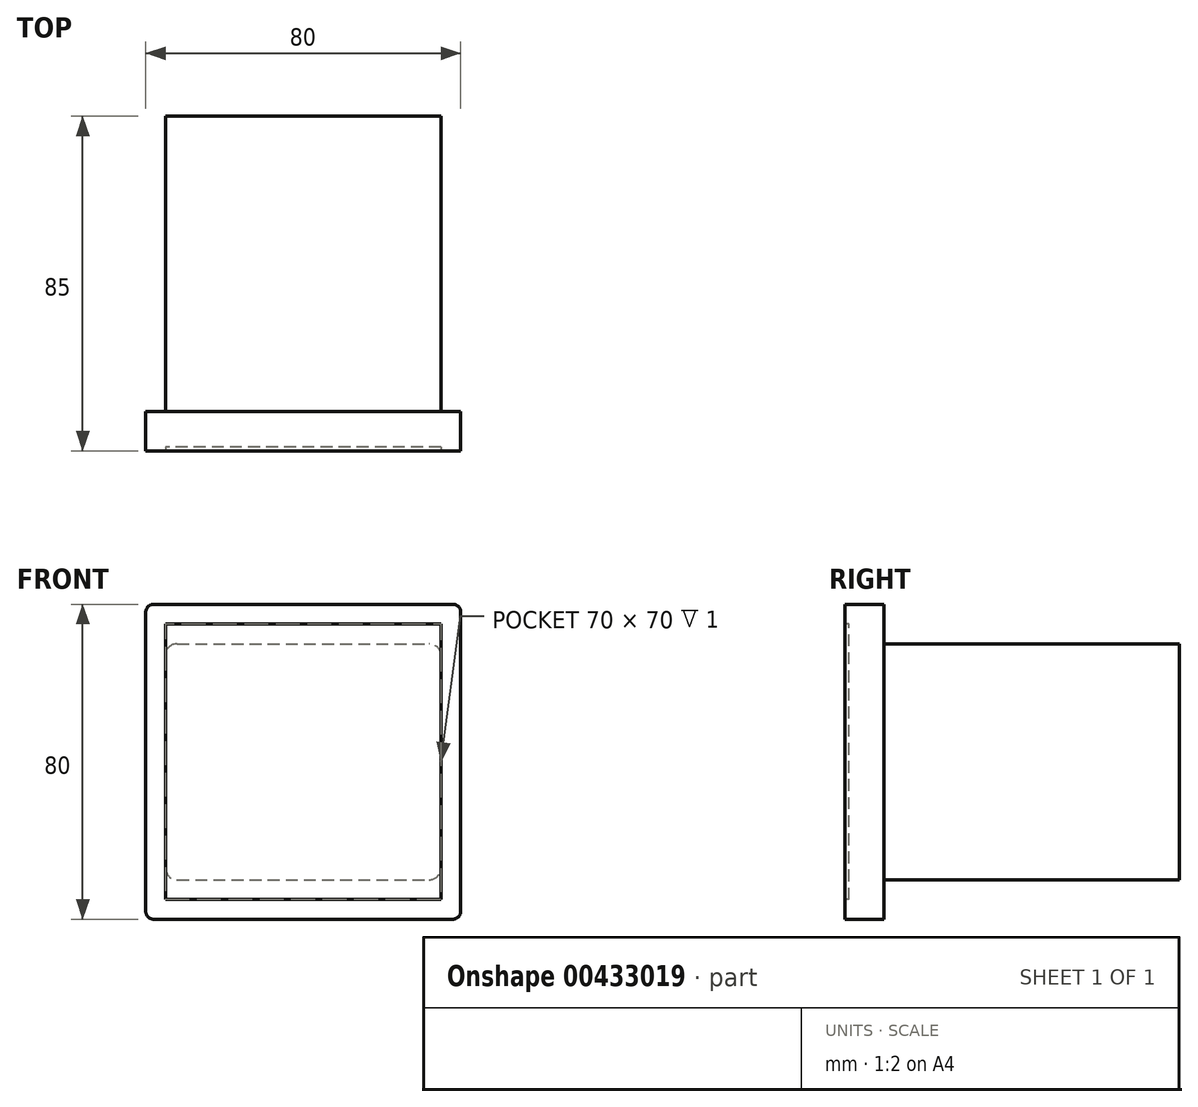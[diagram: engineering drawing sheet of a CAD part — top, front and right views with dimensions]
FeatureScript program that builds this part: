
annotation { "Feature Type Name" : "Feature", "Feature Type Description" : "" }
export const myFeature = defineFeature(function(context is Context, id is Id, definition is map)
    precondition{}
    {
        {
            var Q0;
            Q0=qCreatedBy(makeId("Front.planeOp"),FACE);
            var sketch = newSketch(context, id + "F0", { "sketchPlane" : qUnion([Q0])});
            skLineSegment(sketch, "E0.bottom", {"start": v(40, -40) * mm, "end": v(-40, -40) * mm});
            skLineSegment(sketch, "E0.top", {"start": v(40, 40) * mm, "end": v(-40, 40) * mm});
            skLineSegment(sketch, "E0.left", {"start": v(40, -40) * mm, "end": v(40, 40) * mm});
            skLineSegment(sketch, "E0.right", {"start": v(-40, -40) * mm, "end": v(-40, 40) * mm});
            skPoint(sketch, "E0.middle", {"position": v(0, 0) * mm});
            skSolve(sketch);
        }
        {
            var Q0;
            Q0 = qSketchRegion(id + "F0", true);
            extrude(context, id + "F1", {"entities" : qUnion([Q0]), "depth" : 10 * mm});
        }
        {
            var Q0;
            Q0=makeQuery(id+"F1.opExtrude","SWEPT_EDGE",EDGE,{"disambiguationData":[OSD([sQuery(id+"F0.wireOp",EDGE,"E0.top"),sQuery(id+"F0.wireOp",EDGE,"E0.right")])]});
            var Q1;
            Q1=makeQuery(id+"F1.opExtrude","SWEPT_EDGE",EDGE,{"disambiguationData":[OSD([sQuery(id+"F0.wireOp",EDGE,"E0.top"),sQuery(id+"F0.wireOp",EDGE,"E0.left")])]});
            var Q2;
            Q2=makeQuery(id+"F1.opExtrude","SWEPT_EDGE",EDGE,{"disambiguationData":[OSD([sQuery(id+"F0.wireOp",EDGE,"E0.bottom"),sQuery(id+"F0.wireOp",EDGE,"E0.left")])]});
            var Q3;
            Q3=makeQuery(id+"F1.opExtrude","SWEPT_EDGE",EDGE,{"disambiguationData":[OSD([sQuery(id+"F0.wireOp",EDGE,"E0.bottom"),sQuery(id+"F0.wireOp",EDGE,"E0.right")])]});
            fillet(context, id + "F2", {"entities" : qUnion([Q0, Q1, Q2, Q3]), "radius" : 2 * mm, "tangentPropagation" : true, "allowEdgeOverflow" : false});
        }
        {
            var Q0;
            Q0=makeQuery(id+"F1.opExtrude","CAP_FACE",FACE,{"disambiguationData":[OSD([sQuery(id+"F0.wireOp",EDGE,"E0.bottom"),sQuery(id+"F0.wireOp",EDGE,"E0.top"),sQuery(id+"F0.wireOp",EDGE,"E0.left"),sQuery(id+"F0.wireOp",EDGE,"E0.right")])],"isStart":false});
            var sketch = newSketch(context, id + "F3", { "sketchPlane" : qUnion([Q0])});
            skLineSegment(sketch, "E1.bottom", {"start": v(35, -35) * mm, "end": v(-35, -35) * mm});
            skLineSegment(sketch, "E1.top", {"start": v(35, 35) * mm, "end": v(-35, 35) * mm});
            skLineSegment(sketch, "E1.left", {"start": v(35, -35) * mm, "end": v(35, 35) * mm});
            skLineSegment(sketch, "E1.right", {"start": v(-35, -35) * mm, "end": v(-35, 35) * mm});
            skPoint(sketch, "E1.middle", {"position": v(0, 0) * mm});
            skSolve(sketch);
        }
        {
            var Q0;
            Q0=makeQuery(id+"F3.imprint","IMPRINT",FACE,{"disambiguationData":[TD([[makeQuery(id+"F3.imprint","IMPRINT",EDGE,{"derivedFrom":sQuery(id+"F3.wireOp",EDGE,"E1.bottom")}),-1.0]])]});
            extrude(context, id + "F4", {"entities" : qUnion([Q0]), "operationType" : NewBodyOperationType.REMOVE, "oppositeDirection" : true, "depth" : 1 * mm});
        }
        {
            var Q0;
            Q0=makeQuery(id+"F1.opExtrude","CAP_FACE",FACE,{"disambiguationData":[OSD([sQuery(id+"F0.wireOp",EDGE,"E0.bottom"),sQuery(id+"F0.wireOp",EDGE,"E0.top"),sQuery(id+"F0.wireOp",EDGE,"E0.left"),sQuery(id+"F0.wireOp",EDGE,"E0.right")])],"isStart":true});
            var sketch = newSketch(context, id + "F5", { "sketchPlane" : qUnion([Q0])});
            skLineSegment(sketch, "E2.bottom", {"start": v(35, -30) * mm, "end": v(-35, -30) * mm});
            skLineSegment(sketch, "E2.top", {"start": v(35, 30) * mm, "end": v(-35, 30) * mm});
            skLineSegment(sketch, "E2.left", {"start": v(35, -30) * mm, "end": v(35, 30) * mm});
            skLineSegment(sketch, "E2.right", {"start": v(-35, -30) * mm, "end": v(-35, 30) * mm});
            skPoint(sketch, "E2.middle", {"position": v(0, 0) * mm});
            skSolve(sketch);
        }
        {
            var Q0;
            Q0=makeQuery(id+"F5.imprint","IMPRINT",FACE,{"disambiguationData":[TD([[makeQuery(id+"F5.imprint","IMPRINT",EDGE,{"derivedFrom":sQuery(id+"F5.wireOp",EDGE,"E2.bottom")}),-1.0]])]});
            extrude(context, id + "F6", {"entities" : qUnion([Q0]), "operationType" : NewBodyOperationType.ADD, "depth" : 75 * mm});
        }
        {
            var Q0;
            Q0=makeQuery(id+"F6.opExtrude","SWEPT_EDGE",EDGE,{"disambiguationData":[OSD([sQuery(id+"F5.wireOp",EDGE,"E2.top"),sQuery(id+"F5.wireOp",EDGE,"E2.right")])]});
            var Q1;
            Q1=makeQuery(id+"F6.opExtrude","SWEPT_EDGE",EDGE,{"disambiguationData":[OSD([sQuery(id+"F5.wireOp",EDGE,"E2.top"),sQuery(id+"F5.wireOp",EDGE,"E2.left")])]});
            var Q2;
            Q2=makeQuery(id+"F6.opExtrude","SWEPT_EDGE",EDGE,{"disambiguationData":[OSD([sQuery(id+"F5.wireOp",EDGE,"E2.bottom"),sQuery(id+"F5.wireOp",EDGE,"E2.right")])]});
            var Q3;
            Q3=makeQuery(id+"F6.opExtrude","SWEPT_EDGE",EDGE,{"disambiguationData":[OSD([sQuery(id+"F5.wireOp",EDGE,"E2.bottom"),sQuery(id+"F5.wireOp",EDGE,"E2.left")])]});
            fillet(context, id + "F7", {"entities" : qUnion([Q0, Q1, Q2, Q3]), "radius" : 3 * mm, "tangentPropagation" : true, "allowEdgeOverflow" : false});
        }
    });
